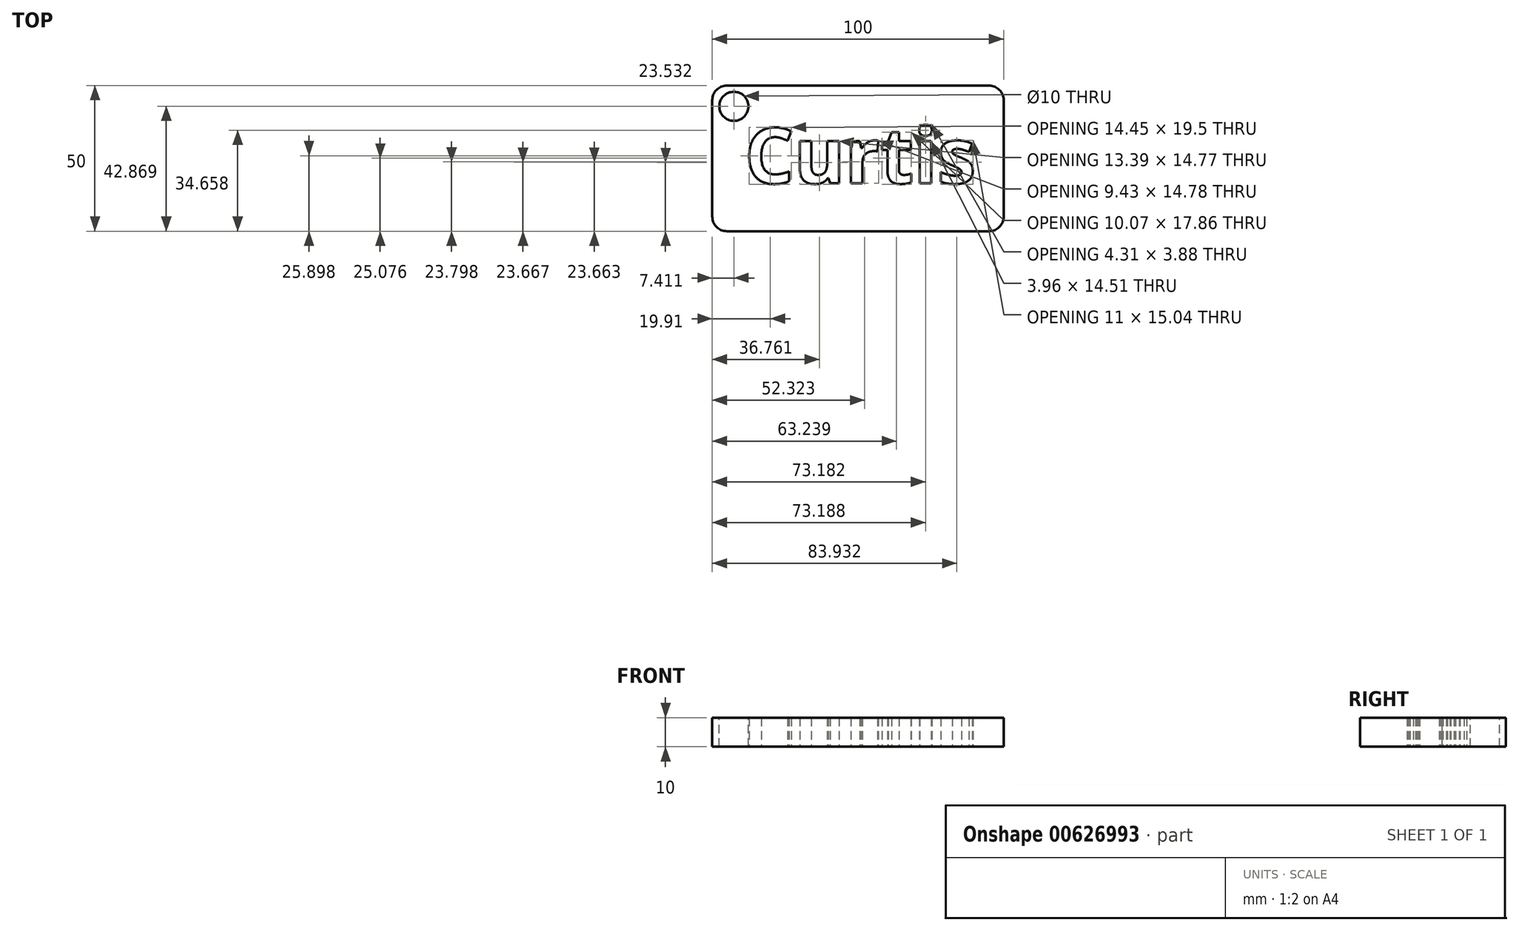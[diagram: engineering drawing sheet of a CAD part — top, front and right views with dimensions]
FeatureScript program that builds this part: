
annotation { "Feature Type Name" : "Feature", "Feature Type Description" : "" }
export const myFeature = defineFeature(function(context is Context, id is Id, definition is map)
    precondition{}
    {
        {
            var Q0;
            Q0=qCreatedBy(makeId("Top.planeOp"),FACE);
            var sketch = newSketch(context, id + "F0", { "sketchPlane" : qUnion([Q0])});
            skLineSegment(sketch, "E0.bottom", {"start": v(-17.21, 32.89) * mm, "end": v(82.79, 32.89) * mm});
            skLineSegment(sketch, "E0.top", {"start": v(-17.21, -17.11) * mm, "end": v(82.79, -17.11) * mm});
            skLineSegment(sketch, "E0.left", {"start": v(-17.21, 32.89) * mm, "end": v(-17.21, -17.11) * mm});
            skLineSegment(sketch, "E0.right", {"start": v(82.79, 32.89) * mm, "end": v(82.79, -17.11) * mm});
            skText(sketch, "E1", { "text": "Curtis\n", "fontName": "OpenSans-Bold.ttf"});
            const initialGuessF0  = {"E1": [-0.00607, -0.0007, 1, 0, 0.01913]};
            skSetInitialGuess(sketch, initialGuessF0);
            skSolve(sketch);
        }
        {
            var Q0;
            Q0 = qSketchRegion(id + "F0", true);
            extrude(context, id + "F1", {"entities" : qUnion([Q0]), "depth" : 10 * mm, "offsetDistance" : 25 * mm});
        }
        {
            var Q0;
            Q0=makeQuery(id+"F1.opExtrude","CAP_FACE",FACE,{"disambiguationData":[OSD([sQuery(id+"F0.wireOp",EDGE,"E0.bottom"),sQuery(id+"F0.wireOp",EDGE,"E0.top"),sQuery(id+"F0.wireOp",EDGE,"E0.left"),sQuery(id+"F0.wireOp",EDGE,"E0.right"),sQuery(id+"F0.wireOp",EDGE,"E1.sketch_text.stroke-0"),sQuery(id+"F0.wireOp",EDGE,"E1.sketch_text.stroke-1"),sQuery(id+"F0.wireOp",EDGE,"E1.sketch_text.stroke-2"),sQuery(id+"F0.wireOp",EDGE,"E1.sketch_text.stroke-3"),sQuery(id+"F0.wireOp",EDGE,"E1.sketch_text.stroke-4"),sQuery(id+"F0.wireOp",EDGE,"E1.sketch_text.stroke-5"),sQuery(id+"F0.wireOp",EDGE,"E1.sketch_text.stroke-6"),sQuery(id+"F0.wireOp",EDGE,"E1.sketch_text.stroke-7"),sQuery(id+"F0.wireOp",EDGE,"E1.sketch_text.stroke-8"),sQuery(id+"F0.wireOp",EDGE,"E1.sketch_text.stroke-9"),sQuery(id+"F0.wireOp",EDGE,"E1.sketch_text.stroke-10"),sQuery(id+"F0.wireOp",EDGE,"E1.sketch_text.stroke-11"),sQuery(id+"F0.wireOp",EDGE,"E1.sketch_text.stroke-12"),sQuery(id+"F0.wireOp",EDGE,"E1.sketch_text.stroke-13"),sQuery(id+"F0.wireOp",EDGE,"E1.sketch_text.stroke-14"),sQuery(id+"F0.wireOp",EDGE,"E1.sketch_text.stroke-15"),sQuery(id+"F0.wireOp",EDGE,"E1.sketch_text.stroke-16"),sQuery(id+"F0.wireOp",EDGE,"E1.sketch_text.stroke-17"),sQuery(id+"F0.wireOp",EDGE,"E1.sketch_text.stroke-18"),sQuery(id+"F0.wireOp",EDGE,"E1.sketch_text.stroke-19"),sQuery(id+"F0.wireOp",EDGE,"E1.sketch_text.stroke-20"),sQuery(id+"F0.wireOp",EDGE,"E1.sketch_text.stroke-21"),sQuery(id+"F0.wireOp",EDGE,"E1.sketch_text.stroke-22"),sQuery(id+"F0.wireOp",EDGE,"E1.sketch_text.stroke-23"),sQuery(id+"F0.wireOp",EDGE,"E1.sketch_text.stroke-24"),sQuery(id+"F0.wireOp",EDGE,"E1.sketch_text.stroke-25"),sQuery(id+"F0.wireOp",EDGE,"E1.sketch_text.stroke-26"),sQuery(id+"F0.wireOp",EDGE,"E1.sketch_text.stroke-27"),sQuery(id+"F0.wireOp",EDGE,"E1.sketch_text.stroke-28"),sQuery(id+"F0.wireOp",EDGE,"E1.sketch_text.stroke-29"),sQuery(id+"F0.wireOp",EDGE,"E1.sketch_text.stroke-30"),sQuery(id+"F0.wireOp",EDGE,"E1.sketch_text.stroke-31"),sQuery(id+"F0.wireOp",EDGE,"E1.sketch_text.stroke-32"),sQuery(id+"F0.wireOp",EDGE,"E1.sketch_text.stroke-33"),sQuery(id+"F0.wireOp",EDGE,"E1.sketch_text.stroke-34"),sQuery(id+"F0.wireOp",EDGE,"E1.sketch_text.stroke-35"),sQuery(id+"F0.wireOp",EDGE,"E1.sketch_text.stroke-36"),sQuery(id+"F0.wireOp",EDGE,"E1.sketch_text.stroke-37"),sQuery(id+"F0.wireOp",EDGE,"E1.sketch_text.stroke-38"),sQuery(id+"F0.wireOp",EDGE,"E1.sketch_text.stroke-39"),sQuery(id+"F0.wireOp",EDGE,"E1.sketch_text.stroke-40"),sQuery(id+"F0.wireOp",EDGE,"E1.sketch_text.stroke-41"),sQuery(id+"F0.wireOp",EDGE,"E1.sketch_text.stroke-42"),sQuery(id+"F0.wireOp",EDGE,"E1.sketch_text.stroke-43"),sQuery(id+"F0.wireOp",EDGE,"E1.sketch_text.stroke-44"),sQuery(id+"F0.wireOp",EDGE,"E1.sketch_text.stroke-45"),sQuery(id+"F0.wireOp",EDGE,"E1.sketch_text.stroke-46"),sQuery(id+"F0.wireOp",EDGE,"E1.sketch_text.stroke-47"),sQuery(id+"F0.wireOp",EDGE,"E1.sketch_text.stroke-48"),sQuery(id+"F0.wireOp",EDGE,"E1.sketch_text.stroke-49"),sQuery(id+"F0.wireOp",EDGE,"E1.sketch_text.stroke-50"),sQuery(id+"F0.wireOp",EDGE,"E1.sketch_text.stroke-51"),sQuery(id+"F0.wireOp",EDGE,"E1.sketch_text.stroke-52"),sQuery(id+"F0.wireOp",EDGE,"E1.sketch_text.stroke-53"),sQuery(id+"F0.wireOp",EDGE,"E1.sketch_text.stroke-54"),sQuery(id+"F0.wireOp",EDGE,"E1.sketch_text.stroke-55"),sQuery(id+"F0.wireOp",EDGE,"E1.sketch_text.stroke-56"),sQuery(id+"F0.wireOp",EDGE,"E1.sketch_text.stroke-57"),sQuery(id+"F0.wireOp",EDGE,"E1.sketch_text.stroke-58"),sQuery(id+"F0.wireOp",EDGE,"E1.sketch_text.stroke-59"),sQuery(id+"F0.wireOp",EDGE,"E1.sketch_text.stroke-60"),sQuery(id+"F0.wireOp",EDGE,"E1.sketch_text.stroke-61"),sQuery(id+"F0.wireOp",EDGE,"E1.sketch_text.stroke-62"),sQuery(id+"F0.wireOp",EDGE,"E1.sketch_text.stroke-63"),sQuery(id+"F0.wireOp",EDGE,"E1.sketch_text.stroke-64"),sQuery(id+"F0.wireOp",EDGE,"E1.sketch_text.stroke-65"),sQuery(id+"F0.wireOp",EDGE,"E1.sketch_text.stroke-66"),sQuery(id+"F0.wireOp",EDGE,"E1.sketch_text.stroke-67"),sQuery(id+"F0.wireOp",EDGE,"E1.sketch_text.stroke-68"),sQuery(id+"F0.wireOp",EDGE,"E1.sketch_text.stroke-69"),sQuery(id+"F0.wireOp",EDGE,"E1.sketch_text.stroke-70"),sQuery(id+"F0.wireOp",EDGE,"E1.sketch_text.stroke-71"),sQuery(id+"F0.wireOp",EDGE,"E1.sketch_text.stroke-72"),sQuery(id+"F0.wireOp",EDGE,"E1.sketch_text.stroke-73"),sQuery(id+"F0.wireOp",EDGE,"E1.sketch_text.stroke-74"),sQuery(id+"F0.wireOp",EDGE,"E1.sketch_text.stroke-75"),sQuery(id+"F0.wireOp",EDGE,"E1.sketch_text.stroke-76"),sQuery(id+"F0.wireOp",EDGE,"E1.sketch_text.stroke-77"),sQuery(id+"F0.wireOp",EDGE,"E1.sketch_text.stroke-78"),sQuery(id+"F0.wireOp",EDGE,"E1.sketch_text.stroke-79"),sQuery(id+"F0.wireOp",EDGE,"E1.sketch_text.stroke-80"),sQuery(id+"F0.wireOp",EDGE,"E1.sketch_text.stroke-81"),sQuery(id+"F0.wireOp",EDGE,"E1.sketch_text.stroke-82"),sQuery(id+"F0.wireOp",EDGE,"E1.sketch_text.stroke-83"),sQuery(id+"F0.wireOp",EDGE,"E1.sketch_text.stroke-84"),sQuery(id+"F0.wireOp",EDGE,"E1.sketch_text.stroke-85"),sQuery(id+"F0.wireOp",EDGE,"E1.sketch_text.stroke-86"),sQuery(id+"F0.wireOp",EDGE,"E1.sketch_text.stroke-87"),sQuery(id+"F0.wireOp",EDGE,"E1.sketch_text.stroke-88"),sQuery(id+"F0.wireOp",EDGE,"E1.sketch_text.stroke-89"),sQuery(id+"F0.wireOp",EDGE,"E1.sketch_text.stroke-90"),sQuery(id+"F0.wireOp",EDGE,"E1.sketch_text.stroke-91"),sQuery(id+"F0.wireOp",EDGE,"E1.sketch_text.stroke-92"),sQuery(id+"F0.wireOp",EDGE,"E1.sketch_text.stroke-93"),sQuery(id+"F0.wireOp",EDGE,"E1.sketch_text.stroke-94"),sQuery(id+"F0.wireOp",EDGE,"E1.sketch_text.stroke-95"),sQuery(id+"F0.wireOp",EDGE,"E1.sketch_text.stroke-96"),sQuery(id+"F0.wireOp",EDGE,"E1.sketch_text.stroke-97")])],"isStart":false});
            var sketch = newSketch(context, id + "F2", { "sketchPlane" : qUnion([Q0])});
            skSolve(sketch);
        }
        {
            var Q0;
            Q0=makeQuery(id+"F2.imprint","IMPRINT",FACE,{"disambiguationData":[TD([[makeQuery(id+"F2.imprint","IMPRINT",EDGE,{"derivedFrom":makeQuery(id+"F1.opExtrude","CAP_EDGE",EDGE,{"disambiguationData":[OSD([sQuery(id+"F0.wireOp",EDGE,"E0.bottom")])],"isStart":false})}),-1.0]])]});
            var sketch = newSketch(context, id + "F3", { "sketchPlane" : qUnion([Q0])});
            skCircle(sketch, "E2", {"center": v(-9.8, 25.76) * mm, "radius": 5 * mm});
            skSolve(sketch);
        }
        {
            var Q0;
            Q0 = qSketchRegion(id + "F3", true);
            extrude(context, id + "F4", {"entities" : qUnion([Q0]), "operationType" : NewBodyOperationType.REMOVE, "endBound" : BoundingType.THROUGH_ALL, "oppositeDirection" : true, "depth" : 25 * mm, "offsetDistance" : 25 * mm});
        }
        {
            var Q0;
            Q0=makeQuery(id+"F1.opExtrude","SWEPT_EDGE",EDGE,{"disambiguationData":[OSD([sQuery(id+"F0.wireOp",EDGE,"E0.bottom"),sQuery(id+"F0.wireOp",EDGE,"E0.left")])]});
            var Q1;
            Q1=makeQuery(id+"F1.opExtrude","SWEPT_EDGE",EDGE,{"disambiguationData":[OSD([sQuery(id+"F0.wireOp",EDGE,"E0.top"),sQuery(id+"F0.wireOp",EDGE,"E0.left")])]});
            fillet(context, id + "F5", {"entities" : qUnion([Q0, Q1]), "radius" : 5 * mm, "tangentPropagation" : true, "allowEdgeOverflow" : false});
        }
        {
            var Q0;
            Q0=makeQuery(id+"F1.opExtrude","SWEPT_EDGE",EDGE,{"disambiguationData":[OSD([sQuery(id+"F0.wireOp",EDGE,"E0.top"),sQuery(id+"F0.wireOp",EDGE,"E0.right")])]});
            fillet(context, id + "F6", {"entities" : qUnion([Q0]), "radius" : 5 * mm, "tangentPropagation" : true, "allowEdgeOverflow" : false});
        }
        {
            var Q0;
            Q0=makeQuery(id+"F1.opExtrude","SWEPT_EDGE",EDGE,{"disambiguationData":[OSD([sQuery(id+"F0.wireOp",EDGE,"E0.bottom"),sQuery(id+"F0.wireOp",EDGE,"E0.right")])]});
            fillet(context, id + "F7", {"entities" : qUnion([Q0]), "radius" : 5 * mm, "tangentPropagation" : true, "allowEdgeOverflow" : false});
        }
    });
